# Revit family: VHE-CE
name_source: partatom
category: Specialty Equipment
units: mm (PartAtom-declared; Revit-internal decimal feet)

## family parameters
Cut with Voids When Loaded = No
Host = Face
Part Type = Normal
Room Calculation Point = No
Round Connector Dimension = Use Diameter
Shared = No

## types (31) — shared parameters
ABAA Compliance = Yes
Assembly Code = C3020200
CE Certification = 0679-CPR-1286
Default Elevation = 0"
Description = CE Marked, EN 1366-4 Tested Watertight movement joint for walls and decks
Durometer Hardness of Silicone Coating (ASTM D2240) = Shore A: 25
European Technical Assessment = ETA-19/0222
Manufacturer = EMSEAL Joint Systems Ltd
Model = Colourseal VHE
Movement (of Nominal Material Size) = +50% / -50%
Product Data URL = https://bit.ly
Product Documentation URL = https://bit.ly
Product Page URL = https://www.emseal.com
R Value Range (ASTM C518) = 2.15 per 1-inch (25mm) depth
Rate of Air Leakage (ASTM E283) = Passed
Resistence to Fire EN 1366-4 - Horizontal = EI45
Resistence to Fire EN 1366-4 -Vertical = EI90
Seal Material Note = Colourseal VHE is coated on the top and bottom with water-resistant Dowsil 790 silicone.
Staining (ASTM C510) = None
Temperature Range (ASTM C711) = 185°F (85°C) to -40°F (-40°C)
Tensile Strength (ASTM D3574) = 18 psi min; 145 kPa
Type Image = VHE-CE.png
URL = http://www.emseal.com

## per-type parameters (varying)
| type | Depth | Quad Bellow | Quint Bellow | Single Bellow | Triple Bellow | Width |
| VHE - .5 inches | 2 3/4" | No | No | Yes | No | 1/2" |
| VHE - .75 inches | 2 3/4" | No | No | Yes | No | 3/4" |
| VHE - 1 inches | 2 3/4" | No | No | Yes | No | 1" |
| VHE - 1.25 inches | 2 3/4" | No | No | Yes | No | 1 1/4" |
| VHE - 1.5 inches | 2 3/4" | No | No | No | Yes | 1 1/2" |
| VHE - 1.75 inches | 2 3/4" | No | No | No | Yes | 1 3/4" |
| VHE - 2 inches | 2 3/4" | No | No | No | Yes | 2" |
| VHE - 2.25 inches | 2 3/4" | No | No | No | Yes | 2 1/4" |
| VHE - 2.5 inches | 2 3/4" | No | No | No | Yes | 2 1/2" |
| VHE - 2.75 inches | 3" | No | No | No | Yes | 2 3/4" |
| VHE - 3 inches | 3 1/2" | No | No | No | Yes | 3" |
| VHE - 3.25 inches | 3 3/4" | Yes | No | No | No | 3 1/4" |
| VHE - 3.5 inches | 3 3/4" | Yes | No | No | No | 3 1/2" |
| VHE - 3.75 inches | 4 1/4" | Yes | No | No | No | 3 3/4" |
| VHE - 4 inches | 4 1/2" | Yes | No | No | No | 4" |
| VHE - 4.25 inches | 4 1/2" | No | Yes | No | No | 4 1/4" |
| VHE - 4.5 inches | 5" | No | Yes | No | No | 4 1/2" |
| VHE - 4.75 inches | 5 1/4" | No | Yes | No | No | 4 3/4" |
| VHE - 5 inches | 5 1/2" | No | Yes | No | No | 5" |
| VHE - 5.25 inches | 5 3/4" | No | Yes | No | No | 5 1/4" |
| VHE - 5.5 inches | 5 3/4" | No | Yes | No | No | 5 1/2" |
| VHE - 5.75 inches | 5 3/4" | No | Yes | No | No | 5 3/4" |
| VHE - 6 inches | 6" | No | Yes | No | No | 6" |
| VHE - 6.25 inches | 6 1/4" | No | Yes | No | No | 6 1/4" |
| VHE - 6.5 inches | 6 1/2" | No | Yes | No | No | 6 1/2" |
| VHE - 6.75 inches | 6 3/4" | No | Yes | No | No | 6 3/4" |
| VHE - 7 inches | 7" | No | Yes | No | No | 7" |
| VHE - 7.25 inches | 7 1/4" | No | Yes | No | No | 7 1/4" |
| VHE - 7.5 inches | 7 1/2" | No | Yes | No | No | 7 1/2" |
| VHE - 7.75 inches | 7 3/4" | No | Yes | No | No | 7 3/4" |
| VHE- 8 inches | 8" | No | Yes | No | No | 8" |

## geometry (parser evidence)
native form markers: Sweep x2
no freeform markers — native parametric forms only
